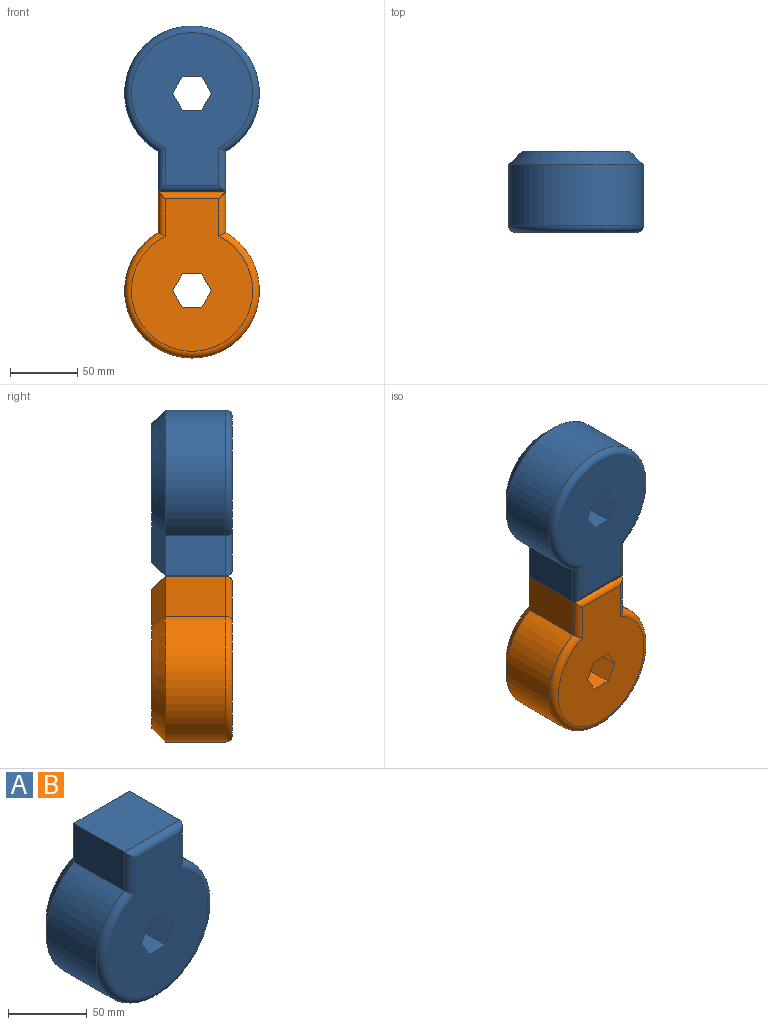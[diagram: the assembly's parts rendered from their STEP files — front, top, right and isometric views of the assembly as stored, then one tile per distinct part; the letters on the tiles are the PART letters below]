
ASSEMBLY  parts=2 mates=1
PART A: 26 faces, bbox 108.2x60x127.4 mm
  f0: plane 45x30mm, normal (-1,0,0), area 1350mm2, adj f1,f9,f12,f22
  f1: cylinder r=50mm len=100mm, axis (0,1,0), area 11781mm2, adj f0,f2,f14,f24
  f2: plane 45x30mm, normal (1,0,0), area 1350mm2, adj f1,f9,f15,f25
  f3: plane 50x14.43mm, normal (0,0,-1), area 721.7mm2, adj f4,f8,f10,f20
  f4: plane 50x12.5mm, normal (-0.87,0,-0.5), area 721.7mm2, adj f3,f5,f10,f21
  f5: plane 50x12.5mm, normal (-0.87,0,0.5), area 721.7mm2, adj f4,f6,f10,f19
  f6: plane 50x14.43mm, normal (0,0,1), area 721.7mm2, adj f5,f7,f10,f17
  f7: plane 50x12.5mm, normal (0.87,0,0.5), area 721.7mm2, adj f6,f8,f10,f16
  f8: plane 50x12.5mm, normal (0.87,0,-0.5), area 721.7mm2, adj f3,f7,f10,f18
  f9: plane 50x45mm, normal (0,0,1), area 2250mm2, adj f0,f2,f13,f23
  f10: plane 113.3x90mm, normal (0,-1,0), area 6813.7mm2, adj f3,f4,f5,f6,f7,f8,f12,f13
  f11: plane 103.3x80mm, normal (0,1,0), area 4000.6mm2, adj f16,f17,f18,f19,f20,f21,f22,f23
  f12: cylinder r=5mm len=32.99mm, axis (0,0,1), area 229.8mm2, adj f0,f10,f13,f14
  f13: cylinder r=5mm len=50mm, axis (1,0,0), area 364.2mm2, adj f9,f10,f12,f15
  f14: torus R=45mm, axis (0,-1,0), area 1997.7mm2, adj f1,f10,f12,f15
  f15: cylinder r=5mm len=32.99mm, axis (0,0,-1), area 229.8mm2, adj f2,f10,f13,f14
  f16: plane 22.5x18.76mm, normal (0.61,0.71,0.35), area 285.8mm2, adj f7,f11,f17,f18
  f17: plane 25.98x10mm, normal (0,0.71,0.71), area 285.8mm2, adj f6,f11,f16,f19
  f18: plane 22.5x18.76mm, normal (0.61,0.71,-0.35), area 285.8mm2, adj f8,f11,f16,f20
  f19: plane 22.5x18.76mm, normal (-0.61,0.71,0.35), area 285.8mm2, adj f5,f11,f17,f21
  f20: plane 25.98x10mm, normal (0,0.71,-0.71), area 285.8mm2, adj f3,f11,f18,f21
  f21: plane 22.5x18.76mm, normal (-0.61,0.71,-0.35), area 285.8mm2, adj f4,f11,f19,f20
  f22: plane 36.22x10mm, normal (-0.71,0.71,0), area 396.4mm2, adj f0,f11,f23,f24
  f23: plane 50x10mm, normal (0,0.71,0.71), area 565.7mm2, adj f9,f11,f22,f25
  f24: cone r=50mm half-angle=45deg, axis (0,-1,0), area 3411.9mm2, adj f1,f11,f22,f25
  f25: plane 36.22x10mm, normal (0.71,0.71,0), area 396.4mm2, adj f2,f11,f23,f24
PART B: same geometry as A
PLACE A rot(axis=(0,1,0),180deg) t=(24.67,21.64,164.87)mm
PLACE B t=(24.67,21.64,18.27)mm fixed
MATE fastened A.f9 <-> B.f9  axis (0,0,-1) through (24.67,19.14,91.57)mm
